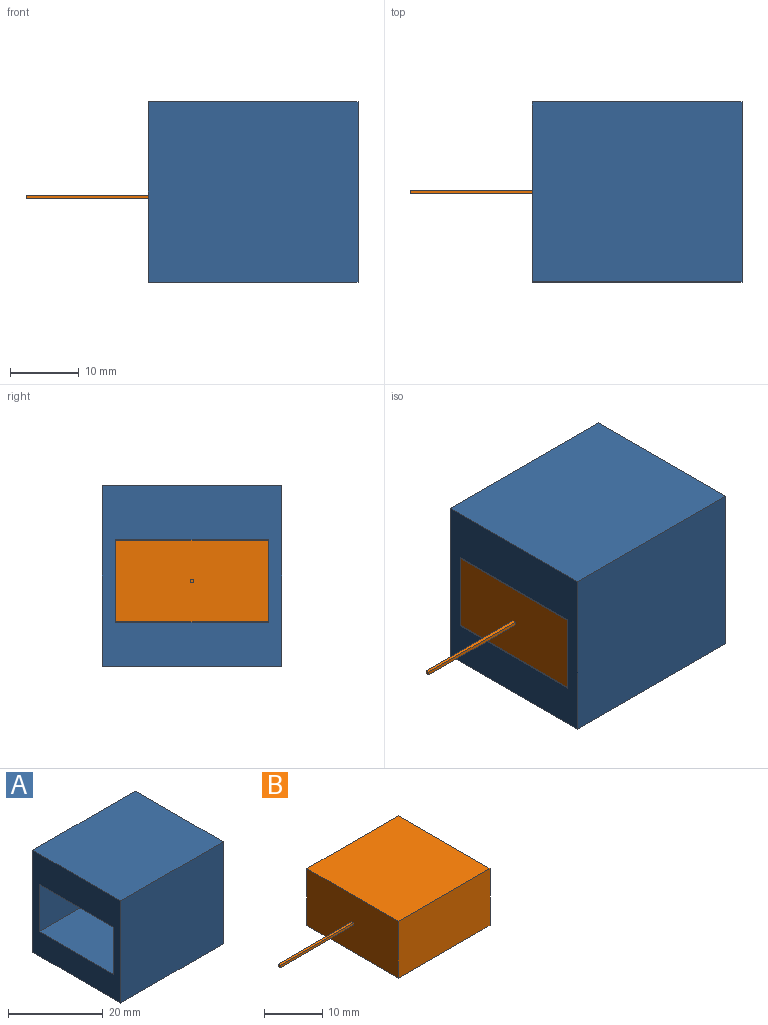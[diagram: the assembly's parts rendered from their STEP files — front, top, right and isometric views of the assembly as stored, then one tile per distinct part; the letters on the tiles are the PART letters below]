
ASSEMBLY  parts=2 mates=1
PART A: 15 faces, bbox 30.6x26.2x26.4 mm
  f0: plane 26.35x26.23mm, normal (-1,0,0), area 420.1mm2, adj f1,f2,f3,f4,f5,f6,f10,f12
  f1: plane 30.58x26.23mm, normal (0,0,1), area 801.8mm2, adj f0,f9,f10,f12
  f2: plane 28.58x22.23mm, normal (0,0,-1), area 635.1mm2, adj f0,f5,f6,f7
  f3: plane 30.58x26.23mm, normal (0,0,-1), area 801.8mm2, adj f0,f9,f10,f12
  f4: plane 28.58x22.23mm, normal (0,0,1), area 635.1mm2, adj f0,f5,f6,f7
  f5: plane 28.58x12.19mm, normal (0,-1,0), area 348.4mm2, adj f0,f2,f4,f7
  f6: plane 28.58x12.19mm, normal (0,1,0), area 348.4mm2, adj f0,f2,f4,f7
  f7: plane 22.23x12.19mm, normal (-1,0,0), area 244.1mm2, adj f2,f4,f5,f6,f8,f11,f13,f14
  f8: plane 5.08x2mm, normal (0,-1,0), area 10.2mm2, adj f7,f9,f13,f14
  f9: plane 26.35x26.23mm, normal (1,0,0), area 664.1mm2, adj f1,f3,f8,f10,f11,f12,f13,f14
  f10: plane 30.58x26.35mm, normal (0,1,0), area 805.7mm2, adj f0,f1,f3,f9
  f11: plane 5.08x2mm, normal (0,1,0), area 10.2mm2, adj f7,f9,f13,f14
  f12: plane 30.58x26.35mm, normal (0,-1,0), area 805.7mm2, adj f0,f1,f3,f9
  f13: plane 5.29x2mm, normal (0,0,1), area 10.6mm2, adj f7,f8,f9,f11
  f14: plane 5.29x2mm, normal (0,0,-1), area 10.6mm2, adj f7,f8,f9,f11
PART B: 11 faces, bbox 40.1x22.2x11.9 mm
  f0: plane 22.23x11.94mm, normal (-1,0,0), area 265.1mm2, adj f1,f2,f4,f5,f6,f8,f9,f10
  f1: plane 22.23x11.94mm, normal (0,1,0), area 265.3mm2, adj f0,f3,f4,f5
  f2: plane 22.23x11.94mm, normal (0,-1,0), area 265.3mm2, adj f0,f3,f4,f5
  f3: plane 22.23x11.94mm, normal (1,0,0), area 265.3mm2, adj f1,f2,f4,f5
  f4: plane 22.23x22.23mm, normal (0,0,1), area 494mm2, adj f0,f1,f2,f3
  f5: plane 22.23x22.23mm, normal (0,0,-1), area 494mm2, adj f0,f1,f2,f3
  f6: plane 17.87x0.51mm, normal (0,1,0), area 9.1mm2, adj f0,f7,f9,f10
  f7: plane 0.51x0.51mm, normal (-1,0,0), area 0.3mm2, adj f6,f8,f9,f10
  f8: plane 17.87x0.51mm, normal (0,-1,0), area 9.1mm2, adj f0,f7,f9,f10
  f9: plane 17.87x0.51mm, normal (0,0,1), area 9.1mm2, adj f0,f6,f7,f8
  f10: plane 17.87x0.51mm, normal (0,0,-1), area 9.1mm2, adj f0,f6,f7,f8
PLACE A t=(0,-2.61,0)mm
PLACE B t=(-9.53,-1.03,6.1)mm
MATE fastened B.f2 <-> A.f6  axis (0,-1,0) through (-20.64,-12.14,6.1)mm
